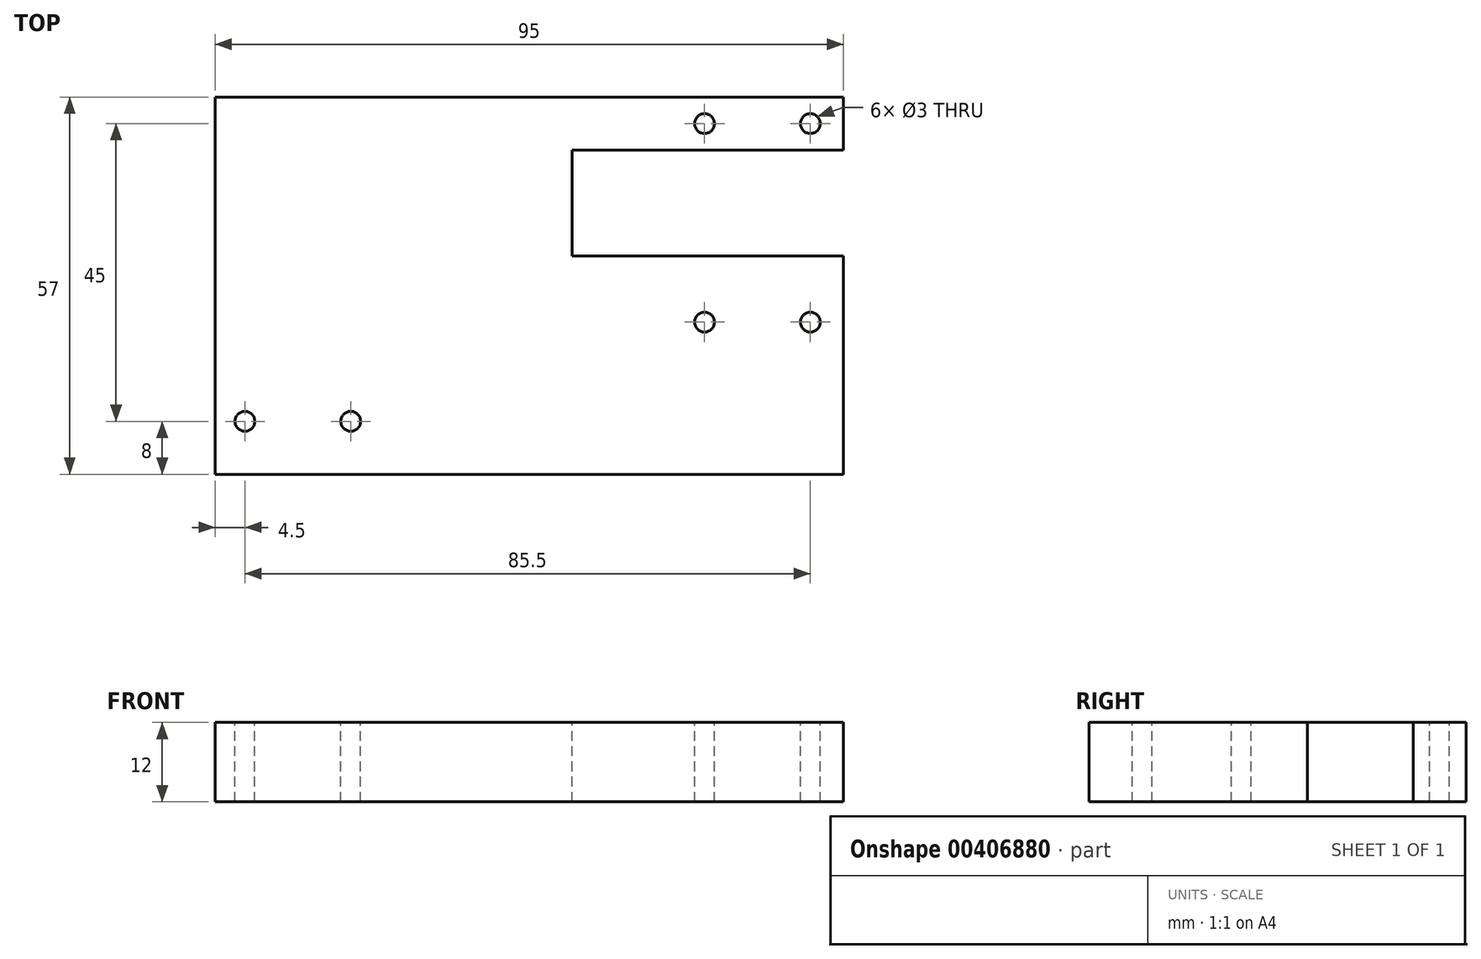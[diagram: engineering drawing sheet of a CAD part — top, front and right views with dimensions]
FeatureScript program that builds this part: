
annotation { "Feature Type Name" : "Feature", "Feature Type Description" : "" }
export const myFeature = defineFeature(function(context is Context, id is Id, definition is map)
    precondition{}
    {
        {
            var Q0;
            Q0=qCreatedBy(makeId("Top.planeOp"),FACE);
            var sketch = newSketch(context, id + "F0", { "sketchPlane" : qUnion([Q0])});
            skLineSegment(sketch, "E0.bottom", {"start": v(47.5, 28.5) * mm, "end": v(-47.5, 28.5) * mm});
            skLineSegment(sketch, "E0.top", {"start": v(47.5, -28.5) * mm, "end": v(-47.5, -28.5) * mm});
            skLineSegment(sketch, "E0.left", {"start": v(47.5, 28.5) * mm, "end": v(47.5, 20.5) * mm});
            skLineSegment(sketch, "E0.right", {"start": v(-47.5, 28.5) * mm, "end": v(-47.5, -28.5) * mm});
            skPoint(sketch, "E0.middle", {"position": v(0, 0) * mm});
            skLineSegment(sketch, "E1", {"start": v(47.5, 20.5) * mm, "end": v(6.5, 20.5) * mm});
            skLineSegment(sketch, "E2", {"start": v(6.5, 20.5) * mm, "end": v(6.5, 4.5) * mm});
            skLineSegment(sketch, "E3", {"start": v(6.5, 4.5) * mm, "end": v(47.5, 4.5) * mm});
            skLineSegment(sketch, "E4.trimOffspring", {"start": v(47.5, 4.5) * mm, "end": v(47.5, -28.5) * mm});
            skSolve(sketch);
        }
        {
            var Q0;
            Q0=makeQuery(id+"F0.imprint","IMPRINT",FACE,{"disambiguationData":[TD([[makeQuery(id+"F0.imprint","IMPRINT",EDGE,{"derivedFrom":sQuery(id+"F0.wireOp",EDGE,"E0.bottom")}),1.0]])]});
            extrude(context, id + "F1", {"entities" : qUnion([Q0]), "endBound" : BoundingType.SYMMETRIC, "oppositeDirection" : true, "depth" : 12 * mm});
        }
        {
            var Q0;
            Q0=makeQuery(id+"F1.opExtrude","CAP_FACE",FACE,{"disambiguationData":[OSD([sQuery(id+"F0.wireOp",EDGE,"E0.bottom"),sQuery(id+"F0.wireOp",EDGE,"E0.top"),sQuery(id+"F0.wireOp",EDGE,"E0.left"),sQuery(id+"F0.wireOp",EDGE,"E0.right"),sQuery(id+"F0.wireOp",EDGE,"E1"),sQuery(id+"F0.wireOp",EDGE,"E2"),sQuery(id+"F0.wireOp",EDGE,"E3"),sQuery(id+"F0.wireOp",EDGE,"E4.trimOffspring")])],"isStart":true});
            var sketch = newSketch(context, id + "F2", { "sketchPlane" : qUnion([Q0])});
            skCircle(sketch, "E5", {"center": v(-43, -20.5) * mm, "radius": 1.5 * mm});
            skCircle(sketch, "E6", {"center": v(-27, -20.5) * mm, "radius": 1.5 * mm});
            skCircle(sketch, "E7", {"center": v(42.5, -5.5) * mm, "radius": 1.5 * mm});
            skCircle(sketch, "E8", {"center": v(26.5, -5.5) * mm, "radius": 1.5 * mm});
            skCircle(sketch, "E9", {"center": v(42.5, 24.5) * mm, "radius": 1.5 * mm});
            skCircle(sketch, "E10", {"center": v(26.5, 24.5) * mm, "radius": 1.5 * mm});
            skSolve(sketch);
        }
        {
            var Q0;
            Q0=makeQuery(id+"F2.imprint","IMPRINT",FACE,{"disambiguationData":[TD([[makeQuery(id+"F2.imprint","IMPRINT",EDGE,{"derivedFrom":sQuery(id+"F2.wireOp",EDGE,"E5")}),1.0]])]});
            var Q1;
            Q1=makeQuery(id+"F2.imprint","IMPRINT",FACE,{"disambiguationData":[TD([[makeQuery(id+"F2.imprint","IMPRINT",EDGE,{"derivedFrom":sQuery(id+"F2.wireOp",EDGE,"E6")}),1.0]])]});
            var Q2;
            Q2=makeQuery(id+"F2.imprint","IMPRINT",FACE,{"disambiguationData":[TD([[makeQuery(id+"F2.imprint","IMPRINT",EDGE,{"derivedFrom":sQuery(id+"F2.wireOp",EDGE,"E8")}),1.0]])]});
            var Q3;
            Q3=makeQuery(id+"F2.imprint","IMPRINT",FACE,{"disambiguationData":[TD([[makeQuery(id+"F2.imprint","IMPRINT",EDGE,{"derivedFrom":sQuery(id+"F2.wireOp",EDGE,"E7")}),1.0]])]});
            var Q4;
            Q4=makeQuery(id+"F2.imprint","IMPRINT",FACE,{"disambiguationData":[TD([[makeQuery(id+"F2.imprint","IMPRINT",EDGE,{"derivedFrom":sQuery(id+"F2.wireOp",EDGE,"E9")}),1.0]])]});
            var Q5;
            Q5=makeQuery(id+"F2.imprint","IMPRINT",FACE,{"disambiguationData":[TD([[makeQuery(id+"F2.imprint","IMPRINT",EDGE,{"derivedFrom":sQuery(id+"F2.wireOp",EDGE,"E10")}),1.0]])]});
            extrude(context, id + "F3", {"entities" : qUnion([Q0, Q1, Q2, Q3, Q4, Q5]), "operationType" : NewBodyOperationType.REMOVE, "oppositeDirection" : true, "depth" : 25 * mm});
        }
    });
